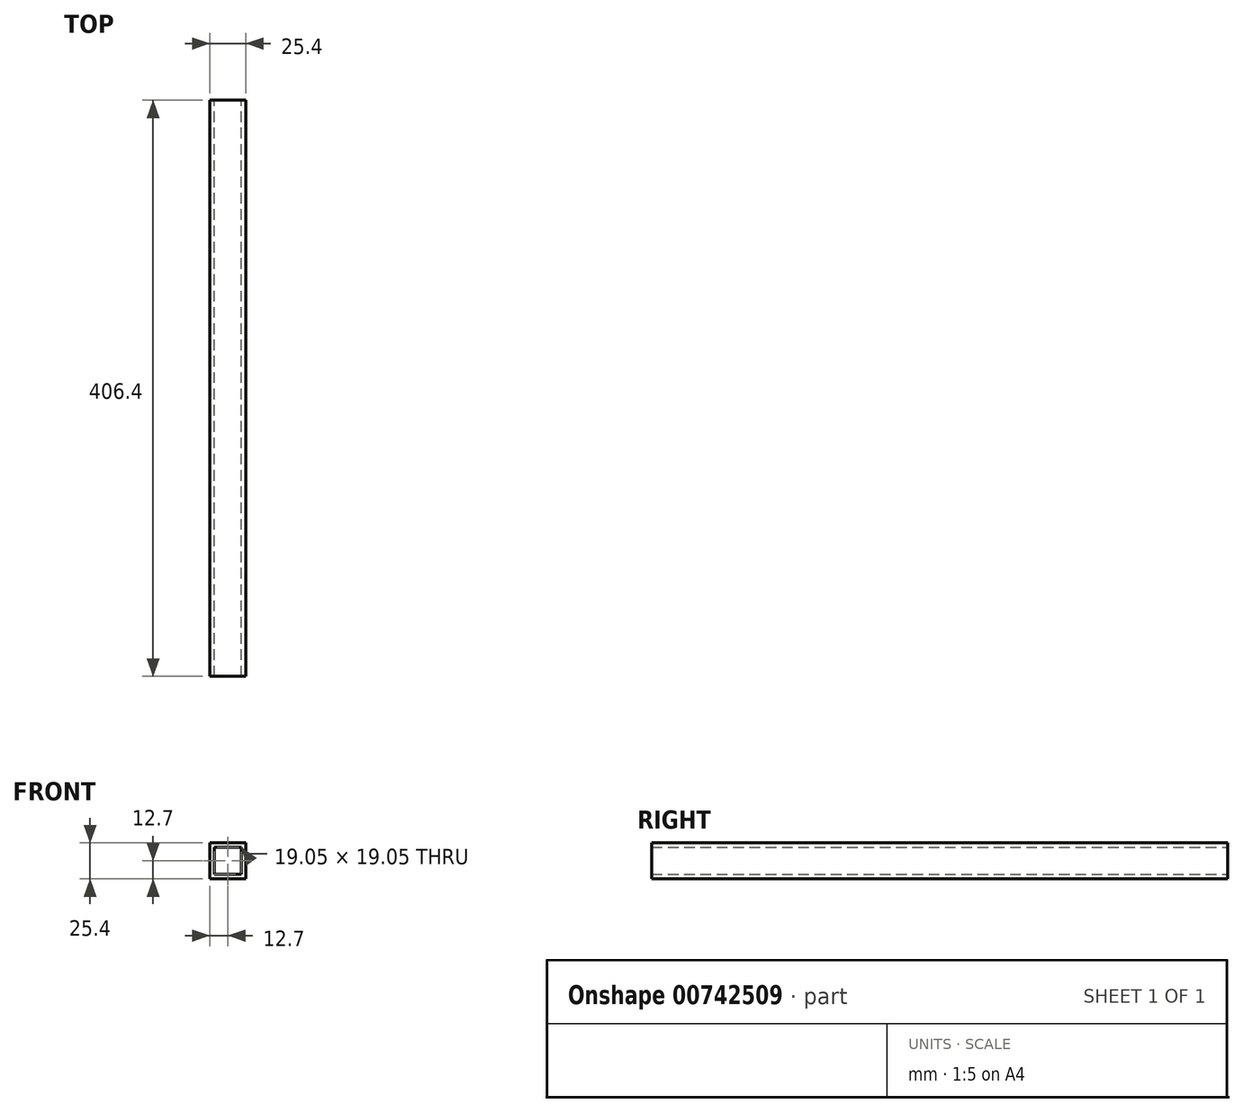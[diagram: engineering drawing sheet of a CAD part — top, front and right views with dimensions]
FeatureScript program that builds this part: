
annotation { "Feature Type Name" : "Feature", "Feature Type Description" : "" }
export const myFeature = defineFeature(function(context is Context, id is Id, definition is map)
    precondition{}
    {
        {
            var Q0;
            Q0=qCreatedBy(makeId("Front.planeOp"),FACE);
            var sketch = newSketch(context, id + "F0", { "sketchPlane" : qUnion([Q0])});
            skLineSegment(sketch, "E0.bottom", {"start": v(12.7, 12.7) * mm, "end": v(-12.7, 12.7) * mm});
            skLineSegment(sketch, "E0.top", {"start": v(12.7, -12.7) * mm, "end": v(-12.7, -12.7) * mm});
            skLineSegment(sketch, "E0.left", {"start": v(12.7, 12.7) * mm, "end": v(12.7, -12.7) * mm});
            skLineSegment(sketch, "E0.right", {"start": v(-12.7, 12.7) * mm, "end": v(-12.7, -12.7) * mm});
            skPoint(sketch, "E0.middle", {"position": v(0, 0) * mm});
            skLineSegment(sketch, "E1.0", {"start": v(9.53, -9.52) * mm, "end": v(-9.53, -9.52) * mm});
            skLineSegment(sketch, "E1.1", {"start": v(9.53, 9.53) * mm, "end": v(9.53, -9.52) * mm});
            skLineSegment(sketch, "E1.2", {"start": v(9.53, 9.53) * mm, "end": v(-9.53, 9.53) * mm});
            skLineSegment(sketch, "E1.3", {"start": v(-9.53, 9.53) * mm, "end": v(-9.53, -9.52) * mm});
            skSolve(sketch);
        }
        {
            var Q0;
            Q0=qSketchRegion(id+"F0",true);
            extrude(context, id + "F1", {"entities" : qUnion([Q0]), "depth" : 406.4 * mm, "offsetDistance" : 25.4 * mm});
        }
    });
